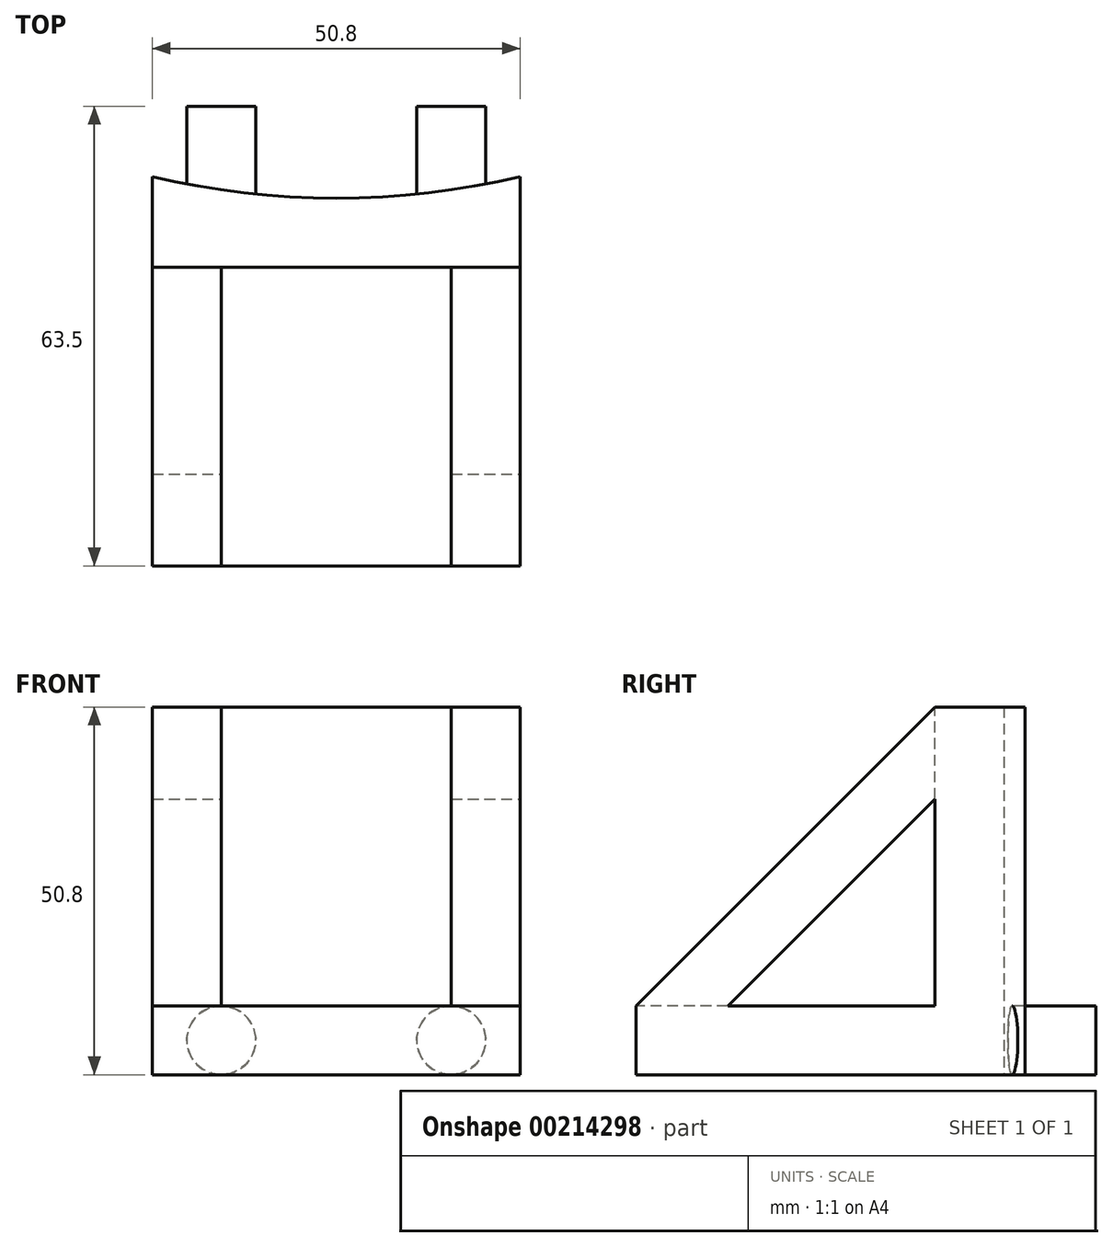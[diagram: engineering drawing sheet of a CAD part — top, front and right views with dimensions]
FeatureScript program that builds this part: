
annotation { "Feature Type Name" : "Feature", "Feature Type Description" : "" }
export const myFeature = defineFeature(function(context is Context, id is Id, definition is map)
    precondition{}
    {
        {
            var Q0;
            Q0=qCreatedBy(makeId("Top.planeOp"),FACE);
            var sketch = newSketch(context, id + "F0", { "sketchPlane" : qUnion([Q0])});
            skLineSegment(sketch, "E0.bottom", {"start": v(25.4, -50.8) * mm, "end": v(-25.4, -50.8) * mm});
            skLineSegment(sketch, "E0.top", {"start": v(25.4, 50.8) * mm, "end": v(-25.4, 50.8) * mm});
            skLineSegment(sketch, "E0.left", {"start": v(25.4, -50.8) * mm, "end": v(25.4, 50.8) * mm});
            skLineSegment(sketch, "E0.right", {"start": v(-25.4, -50.8) * mm, "end": v(-25.4, 50.8) * mm});
            skPoint(sketch, "E0.middle", {"position": v(0, 0) * mm});
            skLineSegment(sketch, "E1", {"start": v(0, 0) * mm, "end": v(0, -50.8) * mm, "construction": true});
            skLineSegment(sketch, "E2", {"start": v(0, 0) * mm, "end": v(0, 111.13) * mm, "construction": true});
            skCircle(sketch, "E3", {"center": v(0, 111.13) * mm, "radius": 111.13 * mm});
            skSolve(sketch);
        }
        {
            var Q0;
            {var subQ0=sQuery(id+"F0.wireOp",EDGE,"E0.bottom");Q0=makeQuery(id+"F0.imprint","IMPRINT",FACE,{"disambiguationData":[TD([[makeQuery(id+"F0.imprint","IMPRINT",EDGE,{"derivedFrom":subQ0}),-1.0]])]});}
            extrude(context, id + "F1", {"entities" : qUnion([Q0]), "depth" : 50.8 * mm});
        }
        {
            var Q0;
            Q0=qCreatedBy(makeId("Right.planeOp"),FACE);
            var sketch = newSketch(context, id + "F2", { "sketchPlane" : qUnion([Q0])});
            skLineSegment(sketch, "E4", {"start": v(0, 0) * mm, "end": v(-50.8, 0) * mm});
            skLineSegment(sketch, "E5", {"start": v(-50.8, 0) * mm, "end": v(-50.8, 9.52) * mm});
            skLineSegment(sketch, "E6", {"start": v(-50.8, 9.52) * mm, "end": v(-9.52, 50.8) * mm});
            skLineSegment(sketch, "E7", {"start": v(-9.53, 50.8) * mm, "end": v(0, 50.8) * mm});
            skLineSegment(sketch, "E8", {"start": v(0, 50.8) * mm, "end": v(0, 0) * mm});
            skLineSegment(sketch, "E9", {"start": v(0, 0) * mm, "end": v(-9.53, 0) * mm, "construction": true});
            skLineSegment(sketch, "E10", {"start": v(-9.53, 0) * mm, "end": v(-9.53, 9.53) * mm, "construction": true});
            skLineSegment(sketch, "E11", {"start": v(-9.52, 9.53) * mm, "end": v(-38.1, 9.52) * mm});
            skLineSegment(sketch, "E12", {"start": v(-38.1, 9.52) * mm, "end": v(-9.53, 38.1) * mm});
            skLineSegment(sketch, "E13", {"start": v(-9.53, 38.1) * mm, "end": v(-9.52, 9.53) * mm});
            skLineSegment(sketch, "E14", {"start": v(-38.1, 9.52) * mm, "end": v(-50.8, 9.52) * mm});
            skLineSegment(sketch, "E15", {"start": v(-9.53, 38.1) * mm, "end": v(-9.52, 50.8) * mm});
            skLineSegment(sketch, "E16", {"start": v(-9.52, 50.8) * mm, "end": v(-50.8, 50.8) * mm});
            skLineSegment(sketch, "E17", {"start": v(-50.8, 50.8) * mm, "end": v(-50.8, 9.52) * mm});
            skSolve(sketch);
        }
        {
            var Q0;
            Q0=makeQuery(id+"F2.imprint","IMPRINT",FACE,{"disambiguationData":[TD([[makeQuery(id+"F2.imprint","IMPRINT",EDGE,{"derivedFrom":sQuery(id+"F2.wireOp",EDGE,"E6")}),-1.0]])]});
            var Q1;
            Q1=makeQuery(id+"F2.imprint","IMPRINT",FACE,{"disambiguationData":[TD([[makeQuery(id+"F2.imprint","IMPRINT",EDGE,{"derivedFrom":sQuery(id+"F2.wireOp",EDGE,"E11")}),-1.0]])]});
            var Q2;
            Q2=makeQuery(id+"F2.imprint","IMPRINT",FACE,{"disambiguationData":[TD([[makeQuery(id+"F2.imprint","IMPRINT",EDGE,{"derivedFrom":sQuery(id+"F2.wireOp",EDGE,"E6")}),1.0]])]});
            extrude(context, id + "F3", {"entities" : qUnion([Q0, Q1, Q2]), "operationType" : NewBodyOperationType.REMOVE, "depth" : 15.88 * mm, "hasSecondDirection" : true, "secondDirectionOppositeDirection" : true, "secondDirectionDepth" : 15.88 * mm});
        }
        {
            var Q0;
            Q0=makeQuery(id+"F2.imprint","IMPRINT",FACE,{"disambiguationData":[TD([[makeQuery(id+"F2.imprint","IMPRINT",EDGE,{"derivedFrom":sQuery(id+"F2.wireOp",EDGE,"E11")}),-1.0]])]});
            var Q1;
            Q1=makeQuery(id+"F2.imprint","IMPRINT",FACE,{"disambiguationData":[TD([[makeQuery(id+"F2.imprint","IMPRINT",EDGE,{"derivedFrom":sQuery(id+"F2.wireOp",EDGE,"E6")}),1.0]])]});
            extrude(context, id + "F4", {"entities" : qUnion([Q0, Q1]), "operationType" : NewBodyOperationType.REMOVE, "oppositeDirection" : true, "depth" : 25.4 * mm, "hasSecondDirection" : true, "secondDirectionOppositeDirection" : false, "secondDirectionDepth" : 25.4 * mm});
        }
        {
            var Q0;
            Q0=qCreatedBy(makeId("Front.planeOp"),FACE);
            var sketch = newSketch(context, id + "F5", { "sketchPlane" : qUnion([Q0])});
            skLineSegment(sketch, "E18", {"start": v(0, 4.76) * mm, "end": v(0, 0) * mm, "construction": true});
            skLineSegment(sketch, "E19", {"start": v(0, 4.76) * mm, "end": v(-15.88, 4.76) * mm, "construction": true});
            skLineSegment(sketch, "E20", {"start": v(0, 4.76) * mm, "end": v(15.88, 4.76) * mm, "construction": true});
            skCircle(sketch, "E21", {"center": v(-15.88, 4.76) * mm, "radius": 4.76 * mm});
            skCircle(sketch, "E22", {"center": v(15.88, 4.76) * mm, "radius": 4.76 * mm});
            skSolve(sketch);
        }
        {
            var Q0;
            Q0 = qSketchRegion(id + "F5", true);
            extrude(context, id + "F6", {"entities" : qUnion([Q0]), "operationType" : NewBodyOperationType.ADD, "oppositeDirection" : true, "depth" : 12.7 * mm});
        }
    });
